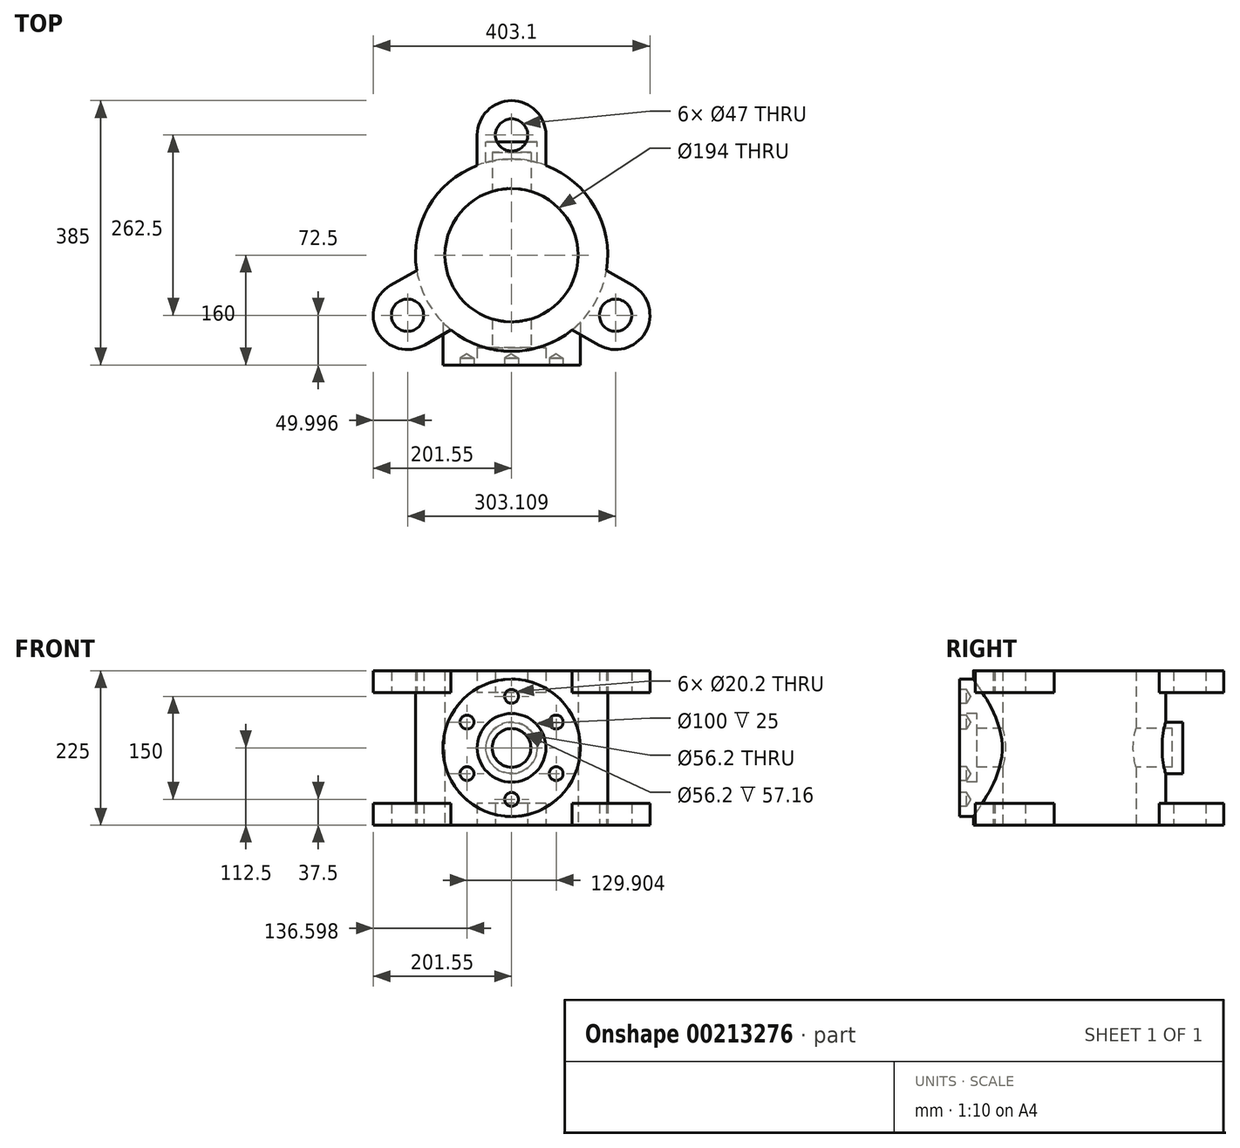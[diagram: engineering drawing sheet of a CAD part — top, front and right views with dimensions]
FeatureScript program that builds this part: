
annotation { "Feature Type Name" : "Feature", "Feature Type Description" : "" }
export const myFeature = defineFeature(function(context is Context, id is Id, definition is map)
    precondition{}
    {
        {
            var Q0;
            Q0=qCreatedBy(makeId("Top.planeOp"),FACE);
            var sketch = newSketch(context, id + "F0", { "sketchPlane" : qUnion([Q0])});
            skArc(sketch, "E0", {"start": v(49.49, 167.86) * mm, "mid": v(0, 225) * mm, "end": v(-49.49, 167.86) * mm});
            skCircle(sketch, "E1", {"center": v(0, 175) * mm, "radius": 23.5 * mm});
            skArc(sketch, "E2.1.0", {"start": v(-170.11, -41.07) * mm, "mid": v(-194.86, -112.5) * mm, "end": v(-120.62, -126.79) * mm});
            skCircle(sketch, "E2.1.1", {"center": v(-151.55, -87.5) * mm, "radius": 23.5 * mm});
            skArc(sketch, "E2.2.0", {"start": v(120.62, -126.79) * mm, "mid": v(194.86, -112.5) * mm, "end": v(170.11, -41.07) * mm});
            skCircle(sketch, "E2.2.1", {"center": v(151.55, -87.5) * mm, "radius": 23.5 * mm});
            skPoint(sketch, "E2.center", {"position": v(0, 0) * mm});
            skCircle(sketch, "E3", {"center": v(0, 0) * mm, "radius": 175 * mm, "construction": true});
            skArc(sketch, "E4", {"start": v(-50, 130.77) * mm, "mid": v(-121.24, 70) * mm, "end": v(-138.25, -22.08) * mm});
            skCircle(sketch, "E5", {"center": v(0, 0) * mm, "radius": 97 * mm});
            skLineSegment(sketch, "E6", {"start": v(-50, 175) * mm, "end": v(-50, 130.77) * mm});
            skLineSegment(sketch, "E7", {"start": v(50, 175) * mm, "end": v(50, 130.77) * mm});
            skLineSegment(sketch, "E8", {"start": v(176.55, -44.2) * mm, "end": v(138.25, -22.08) * mm});
            skLineSegment(sketch, "E9", {"start": v(126.55, -130.8) * mm, "end": v(88.25, -108.68) * mm});
            skLineSegment(sketch, "E10", {"start": v(-176.55, -44.2) * mm, "end": v(-138.25, -22.08) * mm});
            skLineSegment(sketch, "E11", {"start": v(-126.55, -130.8) * mm, "end": v(-88.25, -108.68) * mm});
            skArc(sketch, "E12.trimOffspring", {"start": v(-88.25, -108.68) * mm, "mid": v(0, -140) * mm, "end": v(88.25, -108.68) * mm});
            skArc(sketch, "E13.trimOffspring", {"start": v(138.25, -22.08) * mm, "mid": v(121.24, 70) * mm, "end": v(50, 130.77) * mm});
            skCircle(sketch, "E14", {"center": v(0, 0) * mm, "radius": 140 * mm});
            skSolve(sketch);
        }
        {
            var Q0;
            Q0=makeQuery(id+"F0.imprint","IMPRINT",FACE,{"disambiguationData":[TD([[makeQuery(id+"F0.imprint","IMPRINT",EDGE,{"derivedFrom":sQuery(id+"F0.wireOp",EDGE,"E1")}),-1.0]])]});
            var Q1;
            Q1=makeQuery(id+"F0.imprint","IMPRINT",FACE,{"disambiguationData":[TD([[makeQuery(id+"F0.imprint","IMPRINT",EDGE,{"derivedFrom":sQuery(id+"F0.wireOp",EDGE,"E5")}),-1.0]])]});
            var Q2;
            Q2=makeQuery(id+"F0.imprint","IMPRINT",FACE,{"disambiguationData":[TD([[makeQuery(id+"F0.imprint","IMPRINT",EDGE,{"derivedFrom":sQuery(id+"F0.wireOp",EDGE,"E2.2.1")}),-1.0]])]});
            var Q3;
            Q3=makeQuery(id+"F0.imprint","IMPRINT",FACE,{"disambiguationData":[TD([[makeQuery(id+"F0.imprint","IMPRINT",EDGE,{"derivedFrom":sQuery(id+"F0.wireOp",EDGE,"E2.1.1")}),-1.0]])]});
            extrude(context, id + "F1", {"entities" : qUnion([Q0, Q1, Q2, Q3]), "endBound" : BoundingType.SYMMETRIC, "depth" : 225 * mm});
        }
        {
            var Q0;
            Q0=makeQuery(id+"F0.imprint","IMPRINT",FACE,{"disambiguationData":[TD([[makeQuery(id+"F0.imprint","IMPRINT",EDGE,{"derivedFrom":sQuery(id+"F0.wireOp",EDGE,"E1")}),-1.0]])]});
            var Q1;
            Q1=makeQuery(id+"F0.imprint","IMPRINT",FACE,{"disambiguationData":[TD([[makeQuery(id+"F0.imprint","IMPRINT",EDGE,{"derivedFrom":sQuery(id+"F0.wireOp",EDGE,"E2.1.1")}),-1.0]])]});
            var Q2;
            Q2=makeQuery(id+"F0.imprint","IMPRINT",FACE,{"disambiguationData":[TD([[makeQuery(id+"F0.imprint","IMPRINT",EDGE,{"derivedFrom":sQuery(id+"F0.wireOp",EDGE,"E2.2.1")}),-1.0]])]});
            extrude(context, id + "F2", {"entities" : qUnion([Q0, Q1, Q2]), "operationType" : NewBodyOperationType.REMOVE, "endBound" : BoundingType.SYMMETRIC, "oppositeDirection" : true, "depth" : 161 * mm});
        }
        {
            var Q0;
            Q0=qCreatedBy(makeId("Front.planeOp"),FACE);
            cPlane(context, id + "F3", {"entities" : qUnion([Q0]), "cplaneType" : CPlaneType.OFFSET, "offset" : 160 * mm, "width" : 150 * mm, "height" : 150 * mm});
        }
        {
            var Q0;
            Q0=qCreatedBy(id+"F3.planeOp",FACE);
            var sketch = newSketch(context, id + "F4", { "sketchPlane" : qUnion([Q0])});
            skCircle(sketch, "E15", {"center": v(0, 0) * mm, "radius": 100 * mm});
            skCircle(sketch, "E16", {"center": v(0, 0) * mm, "radius": 50 * mm});
            skCircle(sketch, "E17", {"center": v(0, 75) * mm, "radius": 10.25 * mm});
            skCircle(sketch, "E18.1.0", {"center": v(-64.95, 37.5) * mm, "radius": 10.25 * mm});
            skCircle(sketch, "E18.2.0", {"center": v(-64.95, -37.5) * mm, "radius": 10.25 * mm});
            skCircle(sketch, "E19.1.3.0", {"center": v(0, -75) * mm, "radius": 10.25 * mm});
            skCircle(sketch, "E19.1.4.0", {"center": v(64.95, -37.5) * mm, "radius": 10.25 * mm});
            skCircle(sketch, "E19.1.5.0", {"center": v(64.95, 37.5) * mm, "radius": 10.25 * mm});
            skCircle(sketch, "E20", {"center": v(0, 0) * mm, "radius": 28.1 * mm});
            skSolve(sketch);
        }
        {
            var Q0;
            Q0=makeQuery(id+"F4.imprint","IMPRINT",FACE,{"disambiguationData":[TD([[makeQuery(id+"F4.imprint","IMPRINT",EDGE,{"derivedFrom":sQuery(id+"F4.wireOp",EDGE,"E15")}),1.0]])]});
            var Q1;
            Q1=makeQuery(id+"F4.imprint","IMPRINT",FACE,{"disambiguationData":[TD([[makeQuery(id+"F4.imprint","IMPRINT",EDGE,{"derivedFrom":sQuery(id+"F4.wireOp",EDGE,"E16")}),1.0]])]});
            var Q2;
            Q2=makeQuery(id+"F4.imprint","IMPRINT",FACE,{"disambiguationData":[TD([[makeQuery(id+"F4.imprint","IMPRINT",EDGE,{"derivedFrom":sQuery(id+"F4.wireOp",EDGE,"E18.1.0")}),1.0]])]});
            var Q3;
            Q3=makeQuery(id+"F4.imprint","IMPRINT",FACE,{"disambiguationData":[TD([[makeQuery(id+"F4.imprint","IMPRINT",EDGE,{"derivedFrom":sQuery(id+"F4.wireOp",EDGE,"E17")}),1.0]])]});
            var Q4;
            Q4=makeQuery(id+"F4.imprint","IMPRINT",FACE,{"disambiguationData":[TD([[makeQuery(id+"F4.imprint","IMPRINT",EDGE,{"derivedFrom":sQuery(id+"F4.wireOp",EDGE,"E19.1.5.0")}),1.0]])]});
            var Q5;
            Q5=makeQuery(id+"F4.imprint","IMPRINT",FACE,{"disambiguationData":[TD([[makeQuery(id+"F4.imprint","IMPRINT",EDGE,{"derivedFrom":sQuery(id+"F4.wireOp",EDGE,"E19.1.4.0")}),1.0]])]});
            var Q6;
            Q6=makeQuery(id+"F4.imprint","IMPRINT",FACE,{"disambiguationData":[TD([[makeQuery(id+"F4.imprint","IMPRINT",EDGE,{"derivedFrom":sQuery(id+"F4.wireOp",EDGE,"E19.1.3.0")}),1.0]])]});
            var Q7;
            Q7=makeQuery(id+"F4.imprint","IMPRINT",FACE,{"disambiguationData":[TD([[makeQuery(id+"F4.imprint","IMPRINT",EDGE,{"derivedFrom":sQuery(id+"F4.wireOp",EDGE,"E18.2.0")}),1.0]])]});
            extrude(context, id + "F5", {"entities" : qUnion([Q0, Q1, Q2, Q3, Q4, Q5, Q6, Q7]), "operationType" : NewBodyOperationType.ADD, "endBound" : BoundingType.UP_TO_NEXT, "oppositeDirection" : true, "depth" : 25 * mm});
        }
        {
            var Q0;
            Q0=sQuery(id+"F4.wireOp",VERTEX,"E18.1.0.center");
            var Q1;
            Q1=sQuery(id+"F4.wireOp",VERTEX,"E17.center");
            var Q2;
            Q2=sQuery(id+"F4.wireOp",VERTEX,"E19.1.5.0.center");
            var Q3;
            Q3=sQuery(id+"F4.wireOp",VERTEX,"E19.1.4.0.center");
            var Q4;
            Q4=sQuery(id+"F4.wireOp",VERTEX,"E19.1.3.0.center");
            var Q5;
            Q5=sQuery(id+"F4.wireOp",VERTEX,"E18.2.0.center");
            var Q6;
            Q6=makeQuery(id+"F1.opExtrude","SWEPT_BODY",BODY,{"disambiguationData":[OSD([sQuery(id+"F0.wireOp",EDGE,"E0"),sQuery(id+"F0.wireOp",EDGE,"E1"),sQuery(id+"F0.wireOp",EDGE,"E2.1.0"),sQuery(id+"F0.wireOp",EDGE,"E2.1.1"),sQuery(id+"F0.wireOp",EDGE,"E2.2.0"),sQuery(id+"F0.wireOp",EDGE,"E2.2.1"),sQuery(id+"F0.wireOp",EDGE,"E5"),sQuery(id+"F0.wireOp",EDGE,"E6"),sQuery(id+"F0.wireOp",EDGE,"E7"),sQuery(id+"F0.wireOp",EDGE,"E8"),sQuery(id+"F0.wireOp",EDGE,"E9"),sQuery(id+"F0.wireOp",EDGE,"E10"),sQuery(id+"F0.wireOp",EDGE,"E11"),sQuery(id+"F0.wireOp",EDGE,"E14")])]});
            hole(context, id + "F6", {"style" : HoleStyle.SIMPLE, "endStyle" : HoleEndStyle.BLIND, "holeDiameter" : 20.2 * mm, "holeDepth" : 10 * mm, "startFromSketch" : true, "locations" : qUnion([Q0, Q1, Q2, Q3, Q4, Q5]), "scope" : qUnion([Q6])});
        }
        {
            var Q0;
            Q0=qCreatedBy(makeId("Front.planeOp"),FACE);
            cPlane(context, id + "F7", {"entities" : qUnion([Q0]), "cplaneType" : CPlaneType.OFFSET, "offset" : 165 * mm, "oppositeDirection" : true, "width" : 150 * mm, "height" : 150 * mm});
        }
        {
            var Q0;
            Q0=qCreatedBy(id+"F7.planeOp",FACE);
            var sketch = newSketch(context, id + "F8", { "sketchPlane" : qUnion([Q0])});
            skCircle(sketch, "E21", {"center": v(0, 0) * mm, "radius": 37.5 * mm});
            skSolve(sketch);
        }
        {
            var Q0;
            Q0=makeQuery(id+"F8.imprint","IMPRINT",FACE,{"disambiguationData":[TD([[makeQuery(id+"F8.imprint","IMPRINT",EDGE,{"derivedFrom":sQuery(id+"F8.wireOp",EDGE,"E21")}),1.0]])]});
            extrude(context, id + "F9", {"entities" : qUnion([Q0]), "operationType" : NewBodyOperationType.ADD, "endBound" : BoundingType.UP_TO_NEXT, "depth" : 25 * mm});
        }
        {
            var Q0;
            Q0=makeQuery(id+"F4.imprint","IMPRINT",FACE,{"disambiguationData":[TD([[makeQuery(id+"F4.imprint","IMPRINT",EDGE,{"derivedFrom":sQuery(id+"F4.wireOp",EDGE,"E16")}),1.0]])]});
            extrude(context, id + "F10", {"entities" : qUnion([Q0]), "operationType" : NewBodyOperationType.REMOVE, "oppositeDirection" : true, "depth" : 25 * mm});
        }
        {
            var Q0;
            Q0=makeQuery(id+"F4.imprint","IMPRINT",FACE,{"disambiguationData":[TD([[makeQuery(id+"F4.imprint","IMPRINT",EDGE,{"derivedFrom":sQuery(id+"F4.wireOp",EDGE,"E20")}),1.0]])]});
            extrude(context, id + "F11", {"entities" : qUnion([Q0]), "operationType" : NewBodyOperationType.REMOVE, "oppositeDirection" : true, "depth" : 310 * mm});
        }
    });
